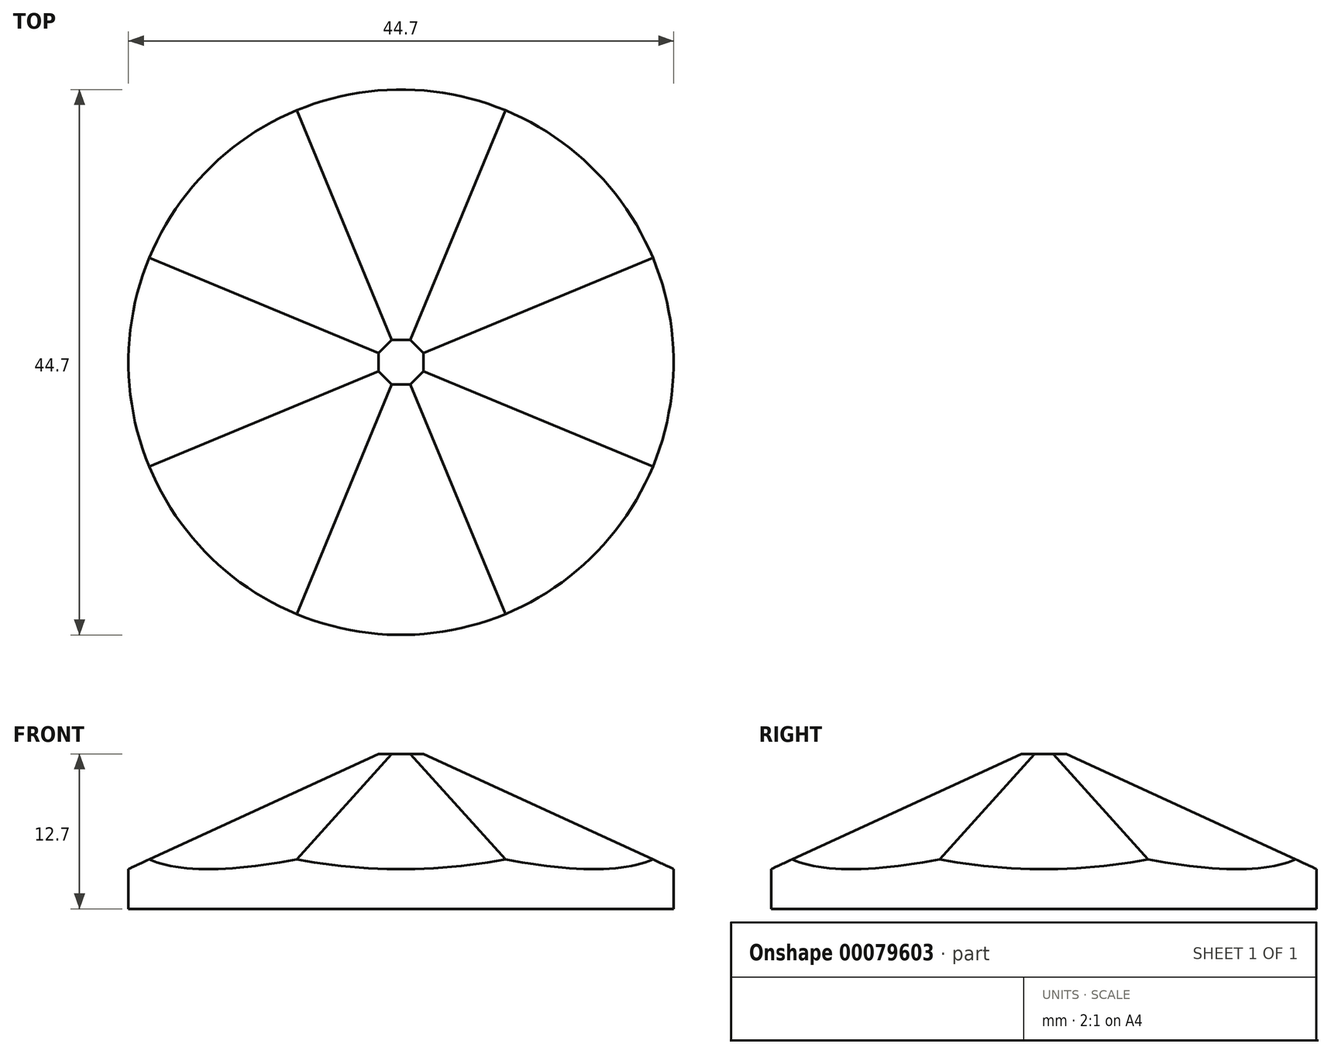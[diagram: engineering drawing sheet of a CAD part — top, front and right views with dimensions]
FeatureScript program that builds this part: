
annotation { "Feature Type Name" : "Feature", "Feature Type Description" : "" }
export const myFeature = defineFeature(function(context is Context, id is Id, definition is map)
    precondition{}
    {
        {
            var Q0;
            Q0=qCreatedBy(makeId("Top.planeOp"),FACE);
            var sketch = newSketch(context, id + "F0", { "sketchPlane" : qUnion([Q0])});
            skCircle(sketch, "E0.cCircle", {"center": v(0, 0) * mm, "radius": 26.67 * mm, "construction": true});
            skLineSegment(sketch, "E0.0", {"start": v(-11.05, 26.67) * mm, "end": v(11.05, 26.67) * mm});
            skLineSegment(sketch, "E0.1", {"start": v(11.05, 26.67) * mm, "end": v(26.67, 11.05) * mm});
            skLineSegment(sketch, "E0.2", {"start": v(26.67, 11.05) * mm, "end": v(26.67, -11.05) * mm});
            skLineSegment(sketch, "E0.3", {"start": v(26.67, -11.05) * mm, "end": v(11.05, -26.67) * mm});
            skLineSegment(sketch, "E0.4", {"start": v(11.05, -26.67) * mm, "end": v(-11.05, -26.67) * mm});
            skLineSegment(sketch, "E0.5", {"start": v(-11.05, -26.67) * mm, "end": v(-26.67, -11.05) * mm});
            skLineSegment(sketch, "E0.6", {"start": v(-26.67, -11.05) * mm, "end": v(-26.67, 11.05) * mm});
            skLineSegment(sketch, "E0.7", {"start": v(-26.67, 11.05) * mm, "end": v(-11.05, 26.67) * mm});
            skPoint(sketch, "E0.0.midPoint", {"position": v(0, 26.67) * mm});
            skSolve(sketch);
        }
        {
            var Q0;
            Q0=qCreatedBy(makeId("Top.planeOp"),FACE);
            cPlane(context, id + "F1", {"entities" : qUnion([Q0]), "cplaneType" : CPlaneType.OFFSET, "offset" : 11.43 * mm, "width" : 152.4 * mm, "height" : 152.4 * mm});
        }
        {
            var Q0;
            Q0=qCreatedBy(id+"F1.planeOp",FACE);
            var sketch = newSketch(context, id + "F2", { "sketchPlane" : qUnion([Q0])});
            skCircle(sketch, "E1.cCircle", {"center": v(0, 0) * mm, "radius": 1.83 * mm, "construction": true});
            skLineSegment(sketch, "E1.0", {"start": v(-0.76, 1.83) * mm, "end": v(0.76, 1.83) * mm});
            skLineSegment(sketch, "E1.1", {"start": v(0.76, 1.83) * mm, "end": v(1.83, 0.76) * mm});
            skLineSegment(sketch, "E1.2", {"start": v(1.83, 0.76) * mm, "end": v(1.83, -0.76) * mm});
            skLineSegment(sketch, "E1.3", {"start": v(1.83, -0.76) * mm, "end": v(0.76, -1.83) * mm});
            skLineSegment(sketch, "E1.4", {"start": v(0.76, -1.83) * mm, "end": v(-0.76, -1.83) * mm});
            skLineSegment(sketch, "E1.5", {"start": v(-0.76, -1.83) * mm, "end": v(-1.83, -0.76) * mm});
            skLineSegment(sketch, "E1.6", {"start": v(-1.83, -0.76) * mm, "end": v(-1.83, 0.76) * mm});
            skLineSegment(sketch, "E1.7", {"start": v(-1.83, 0.76) * mm, "end": v(-0.76, 1.83) * mm});
            skPoint(sketch, "E1.0.midPoint", {"position": v(0, 1.83) * mm});
            skSolve(sketch);
        }
        {
            var Q0;
            Q0 = qSketchRegion(id + "F0", true);
            var Q1;
            Q1 = qSketchRegion(id + "F2", true);
            loft(context, id + "F3", {"sheetProfilesArray" : [{ "sheetProfileEntities" : qUnion([Q0]) }, { "sheetProfileEntities" : qUnion([Q1]) }]});
        }
        {
            var Q0;
            Q0=makeQuery(id+"F3.opLoft","CAP_FACE",FACE,{"disambiguationData":[OSD([makeQuery(id+"F0.imprint","IMPRINT",FACE,{"disambiguationData":[TD([[makeQuery(id+"F0.imprint","IMPRINT",EDGE,{"derivedFrom":sQuery(id+"F0.wireOp",EDGE,"E0.0")}),-1.0]])]})])],"isStart":true});
            var sketch = newSketch(context, id + "F4", { "sketchPlane" : qUnion([Q0])});
            skCircle(sketch, "E2", {"center": v(0, 0) * mm, "radius": 22.35 * mm});
            skSolve(sketch);
        }
        {
            var Q0;
            Q0 = qSketchRegion(id + "F4", true);
            extrude(context, id + "F5", {"entities" : qUnion([Q0]), "operationType" : NewBodyOperationType.ADD, "depth" : 1.27 * mm});
        }
        {
            var Q0;
            Q0=qCreatedBy(makeId("Top.planeOp"),FACE);
            var sketch = newSketch(context, id + "F6", { "sketchPlane" : qUnion([Q0])});
            skCircle(sketch, "E3", {"center": v(0, 0) * mm, "radius": 22.35 * mm});
            skCircle(sketch, "E4", {"center": v(0, 0) * mm, "radius": 33.97 * mm});
            skSolve(sketch);
        }
        {
            var Q0;
            Q0 = qSketchRegion(id + "F6", true);
            extrude(context, id + "F7", {"entities" : qUnion([Q0]), "operationType" : NewBodyOperationType.REMOVE, "depth" : 25.4 * mm});
        }
    });
